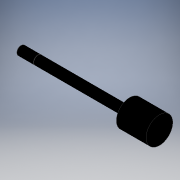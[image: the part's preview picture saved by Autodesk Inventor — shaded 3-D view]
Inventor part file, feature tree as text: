
AUTODESK INVENTOR PART (.ipt)
format: ipt  version: 2019 (Build 230136000, 136)  size: 163,328 bytes
history: native  units: in
note: dims shown in document units (in); Inventor stores cm internally (conversion verified against a paired STEP export)
features: other x70, revolve x3, sketch x3
ambient origin geometry x8: Origin, YZ Plane, XZ Plane, XY Plane, X Axis, Y Axis, Z Axis, Center Point
bodies: Solid1 (feature_tree)
feature tree (76):
  revolve  "Revolution1"  Angle=360.0deg
  revolve  "Revolution2"  [1 undecoded]
  revolve  "Revolution3"  [1 undecoded]
  other  "dia1_XY"
  other  "dia1_YZ"
  other  "dia1_ZX"
  other  "dia1_X"
  other  "dia1_Y"
  other  "dia1_Z"
  other  "dia1_Center"
  other  "dia12_XY"
  other  "dia12_YZ"
  other  "dia12_ZX"
  other  "dia12_X"
  other  "dia12_Y"
  other  "dia12_Z"
  other  "dia12_Center"
  other  "dia2_XY"
  other  "dia2_YZ"
  other  "dia2_ZX"
  other  "dia2_X"
  other  "dia2_Y"
  other  "dia2_Z"
  other  "dia2_Center"
  other  "dia22_XY"
  other  "dia22_YZ"
  other  "dia22_ZX"
  other  "dia22_X"
  other  "dia22_Y"
  other  "dia22_Z"
  other  "dia22_Center"
  other  "rl1_XY"
  other  "rl1_YZ"
  other  "rl1_ZX"
  other  "rl1_X"
  other  "rl1_Y"
  other  "rl1_Z"
  other  "rl1_Center"
  other  "rl2_XY"
  other  "rl2_YZ"
  other  "rl2_ZX"
  other  "rl2_X"
  other  "rl2_Y"
  other  "rl2_Z"
  other  "rl2_Center"
  other  "rod_cp_XY"
  other  "rod_cp_YZ"
  other  "rod_cp_ZX"
  other  "rod_cp_X"
  other  "rod_cp_Y"
  other  "rod_cp_Z"
  other  "rod_cp_Center"
  other  "thd1_XY"
  other  "thd1_YZ"
  other  "thd1_ZX"
  other  "thd1_X"
  other  "thd1_Y"
  other  "thd1_Z"
  other  "thd1_Center"
  other  "thd2_XY"
  other  "thd2_YZ"
  other  "thd2_ZX"
  other  "thd2_X"
  other  "thd2_Y"
  other  "thd2_Z"
  other  "thd2_Center"
  other  "to_rod_clevis_XY"
  other  "to_rod_clevis_YZ"
  other  "to_rod_clevis_ZX"
  other  "to_rod_clevis_X"
  other  "to_rod_clevis_Y"
  other  "to_rod_clevis_Z"
  other  "to_rod_clevis_Center"
  sketch  "Sketch_1"  dims[d0=360.0deg d1=360.0deg]
  sketch  "Sketch_3"  dims[d2=360.0deg]
  sketch  "Sketch_30"  dims[d3=0.0in d4=0.0in d5=0.0in d6=0.0in d7=0.0in]
note: 2 required parameter values undecoded (feature->parameter linkage not recoverable at this tier; creation-order binding heuristic only, values carry confidence <= 0.55)
